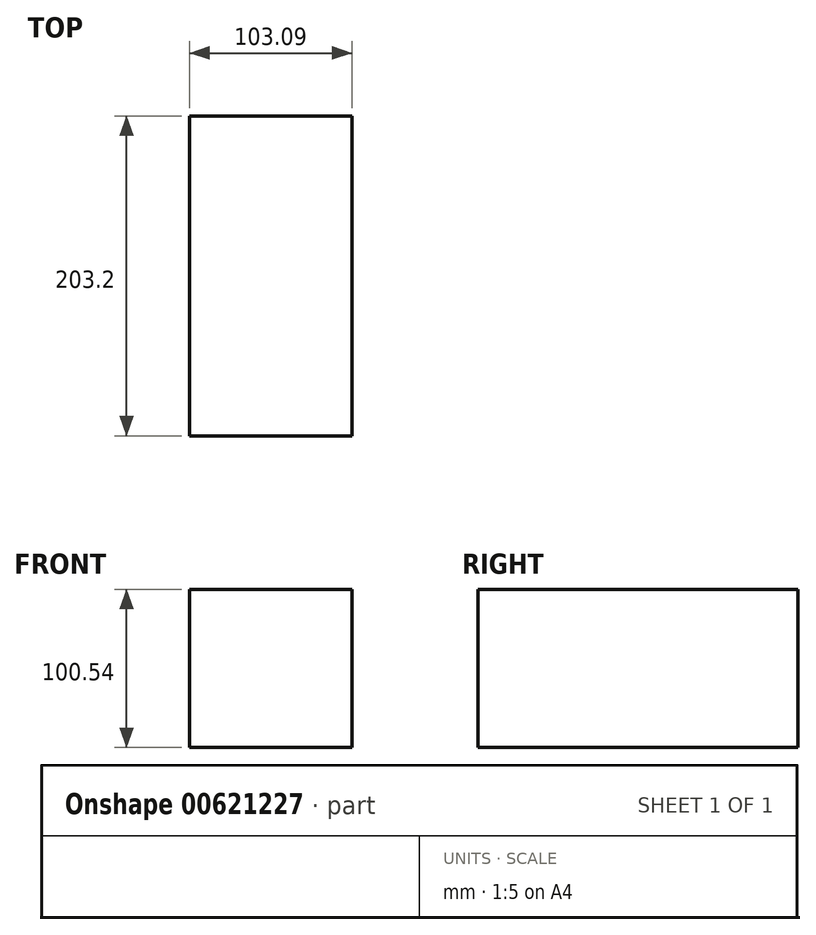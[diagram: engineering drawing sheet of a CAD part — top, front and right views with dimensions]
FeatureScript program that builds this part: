
annotation { "Feature Type Name" : "Feature", "Feature Type Description" : "" }
export const myFeature = defineFeature(function(context is Context, id is Id, definition is map)
    precondition{}
    {
        {
            var Q0;
            Q0=qCreatedBy(makeId("Front.planeOp"),FACE);
            var sketch = newSketch(context, id + "F0", { "sketchPlane" : qUnion([Q0])});
            skLineSegment(sketch, "E0.bottom", {"start": v(-56.3, 60.8) * mm, "end": v(46.78, 60.8) * mm});
            skLineSegment(sketch, "E0.top", {"start": v(-56.3, -39.74) * mm, "end": v(46.78, -39.74) * mm});
            skLineSegment(sketch, "E0.left", {"start": v(-56.3, 60.8) * mm, "end": v(-56.3, -39.74) * mm});
            skLineSegment(sketch, "E0.right", {"start": v(46.78, 60.8) * mm, "end": v(46.78, -39.74) * mm});
            skLineSegment(sketch, "E1.bottom", {"start": v(46.78, -39.74) * mm, "end": v(83.81, -39.74) * mm});
            skLineSegment(sketch, "E1.top", {"start": v(46.78, 54.44) * mm, "end": v(83.81, 54.44) * mm});
            skLineSegment(sketch, "E1.left", {"start": v(46.78, -39.74) * mm, "end": v(46.78, 54.44) * mm});
            skLineSegment(sketch, "E1.right", {"start": v(83.81, -39.74) * mm, "end": v(83.81, 54.44) * mm});
            skSolve(sketch);
        }
        {
            var Q0;
            Q0=makeQuery(id+"F0.imprint","IMPRINT",FACE,{"disambiguationData":[TD([[makeQuery(id+"F0.imprint","IMPRINT",EDGE,{"derivedFrom":sQuery(id+"F0.wireOp",EDGE,"E0.bottom")}),-1.0]])]});
            extrude(context, id + "F1", {"entities" : qUnion([Q0]), "oppositeDirection" : true, "depth" : 101.6 * mm, "offsetDistance" : 25.4 * mm, "hasSecondDirection" : true, "secondDirectionOppositeDirection" : false, "secondDirectionDepth" : 101.6 * mm});
        }
    });
